# Revit family: 276177xx0--Neo Daiquiri 1500x750 Superslim acrylic shower tray with waste kit - Neo Daiquiri - Roca - 276177xx0
name_source: partatom
category: Plumbing Fixtures
units: mm (PartAtom-declared; Revit-internal decimal feet)

## family parameters
Cut with Voids When Loaded = No
Host = Face
OmniClass Number = 23.65.00.00
OmniClass Title = Supply and Distribution of Liquids and Gases
Part Type = Normal
Room Calculation Point = No
Round Connector Dimension = Use Diameter
Shared = No

## types (3) — shared parameters
BIMobject category = Shower trays
Depth = 1500.00
Description = Superslim acrylic shower tray with waste kit
Drain diameter (mm) = 90 mm  [stored 0.295276 ft]
Eco green certification = No
Edition number = 0
Height = 40 mm  [stored 0.131234 ft]
IFC Classification = Furnishing Element
Installation instructions = http://www.roca.com
Length = 1500 mm  [stored 4.92126 ft]
Manufacturer name = Roca
Manufacturer url = http://www.roca.com
Model = 276177..0
NBS Reference Code = 35-06-84
NBS Reference Description = Shower Trays
Nominal height = 40.00
Nominal width = 750.00
Outlet Diameter = 90 mm  [stored 0.295276 ft]
Product Guid = 7c5e816f-c7aa-4c37-adbf-e8b94cac0744
Product data url = http://roca.bimobject.com
Product family = Neo Daiquiri
Product group = SHOWER TRAYS
QR code = https://www.roca.com
Shape = Rectangular
Shape: Rectangular
Suitable for Children = No
Suitable for Handicapped = No
UNSPSC Code = 301815
UNSPSC name = Sanitary ware
URL = http://www.roca.com
Uniclass 1.4 Code = L72143
Uniclass 1.4 Description = Shower trays
Uniclass 2.0 Code = PR-35-06-84
Uniclass 2.0 Description = Shower Trays
Weight Net (Kg) = 0
Width = 750 mm  [stored 2.46063 ft]
zero-valued in all types: Default Elevation

## per-type parameters (varying)
| type | Product SKU |
| White - Neo Daiquiri - Roca | A276177000 |
| Pergamon - Neo Daiquiri - Roca | A276177170 |
| Edelweiss - Neo Daiquiri - Roca | A276177910 |

note: column(s) folded — value = type name in every type: Material

note: [stored X ft] marks values corroborated as IEEE doubles in the binary element streams (Revit-internal decimal feet)

## geometry (parser evidence)
native form markers: Blend x2, Sweep x1
no freeform markers — native parametric forms only
